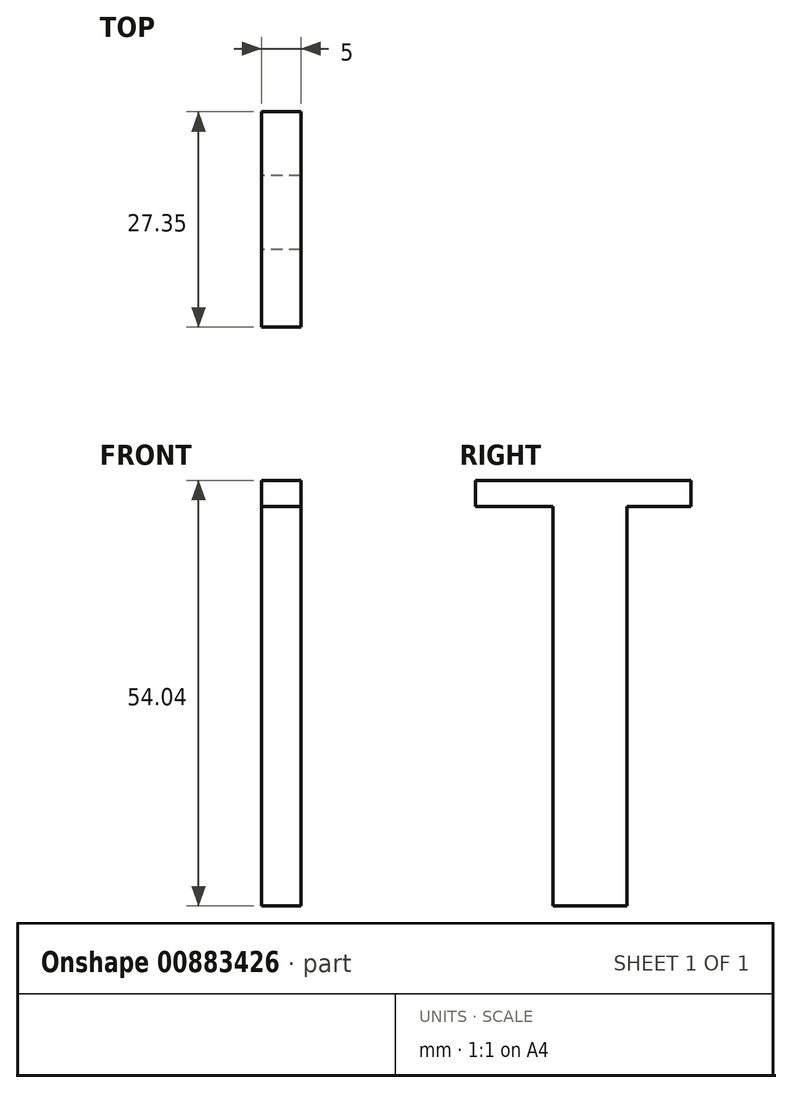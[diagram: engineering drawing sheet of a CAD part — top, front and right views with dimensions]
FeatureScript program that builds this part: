
annotation { "Feature Type Name" : "Feature", "Feature Type Description" : "" }
export const myFeature = defineFeature(function(context is Context, id is Id, definition is map)
    precondition{}
    {
        {
            var Q0;
            Q0=qCreatedBy(makeId("Right.planeOp"),FACE);
            var sketch = newSketch(context, id + "F0", { "sketchPlane" : qUnion([Q0])});
            skLineSegment(sketch, "E0.bottom", {"start": v(4.7, -27.02) * mm, "end": v(-4.7, -27.02) * mm});
            skLineSegment(sketch, "E0.top", {"start": v(4.7, 27.02) * mm, "end": v(-4.7, 27.02) * mm});
            skLineSegment(sketch, "E0.left", {"start": v(4.7, -27.02) * mm, "end": v(4.7, 23.73) * mm});
            skLineSegment(sketch, "E0.right", {"start": v(-4.7, -27.02) * mm, "end": v(-4.7, 23.73) * mm});
            skPoint(sketch, "E0.middle", {"position": v(0, 0) * mm});
            skLineSegment(sketch, "E1", {"start": v(-4.7, 27.02) * mm, "end": v(-14.55, 27.02) * mm});
            skLineSegment(sketch, "E2", {"start": v(-14.55, 27.02) * mm, "end": v(-14.55, 23.73) * mm});
            skLineSegment(sketch, "E3", {"start": v(-14.55, 23.73) * mm, "end": v(-4.7, 23.73) * mm});
            skLineSegment(sketch, "E4", {"start": v(12.8, 23.73) * mm, "end": v(12.8, 27.02) * mm});
            skLineSegment(sketch, "E5", {"start": v(12.8, 27.02) * mm, "end": v(4.7, 27.02) * mm});
            skLineSegment(sketch, "E6.trimOffspring", {"start": v(4.7, 23.73) * mm, "end": v(12.8, 23.73) * mm});
            skSolve(sketch);
        }
        {
            var Q0;
            Q0=makeQuery(id+"F0.imprint","IMPRINT",FACE,{"disambiguationData":[TD([[makeQuery(id+"F0.imprint","IMPRINT",EDGE,{"derivedFrom":sQuery(id+"F0.wireOp",EDGE,"E0.bottom")}),-1.0]])]});
            extrude(context, id + "F1", {"entities" : qUnion([Q0]), "depth" : 5 * mm, "offsetDistance" : 25 * mm});
        }
    });
